# Revit family: kawneer-360_insulclad-sgl_20623
name_source: partatom
category: Doors
revit_build: Autodesk Revit 2015 (Build: 20140905_0730(x64)
units: mm (PartAtom-declared; Revit-internal decimal feet)

## types (1)
- kawneer-360_insulclad-sgl_20623
    2-Color Option = yes
    Air Infiltration (ASTM E 283) = < 0.50 cfm/ft2  @ 6.24 psf (300 Pa), Single Doors,
    Application = moderate traffic, thermal
    Assembly Code = B2030110
    CSI Masterformat Code = 08 41 13
    Cladding Type = Aluminum - ASTM B 221 - 6063-T6 alloy and temper
    Color = any
    Depth = 0"
    Description = The "360 Insulclad" is a narrow stile entrance door that is thermally broken and features the dual moment corner construction.
    Door Corner Construction = Welded
    Door Handle Material = <By Category>
    Door Opening = 0"
    Door Panel Height = 0"
    Door Panel Material = <By Category>
    Door Panel Width = 0"
    Function = Interior
    Function (Interior or Exterior) = Exterior
    Glass Capture = Captured
    Glass Installtion = outside
    Glass U-Factor = product not tested
    Glazing Thickness = 0"
    Hinging Types = Offset Pivot, Butt Hinge, Continuous Gear Hinge
    Hurricane Resistant Tested = product not tested
    Keywords = Entrance, Door, Swing Door, Thermally Broken
    Manufacturer = Kawneer
    Manufacturer Part Number = 360 Insulclad®
    Model = 360 Insulclad®
    Overall U-Factor = product not tested
    Panel Inserts Material = <By Category>
    Product data url = https://bimobject.com
    Short Description = Medium Stile Insulated Swing Door
    Sightline = 0"
    Thermal Transmittance = < 0.67 BTU/hr/sf/F
    Thickness = 0"
    Type Comments = Medium Stile Insulated Swing Door
    Type of Glazing = insulating
    URL = http://www.kawneer.com
    Water - Static (ASTM E 331) = product not tested
    Width = 0"

## geometry (parser evidence)
native form markers: Sweep x11
no freeform markers — native parametric forms only
